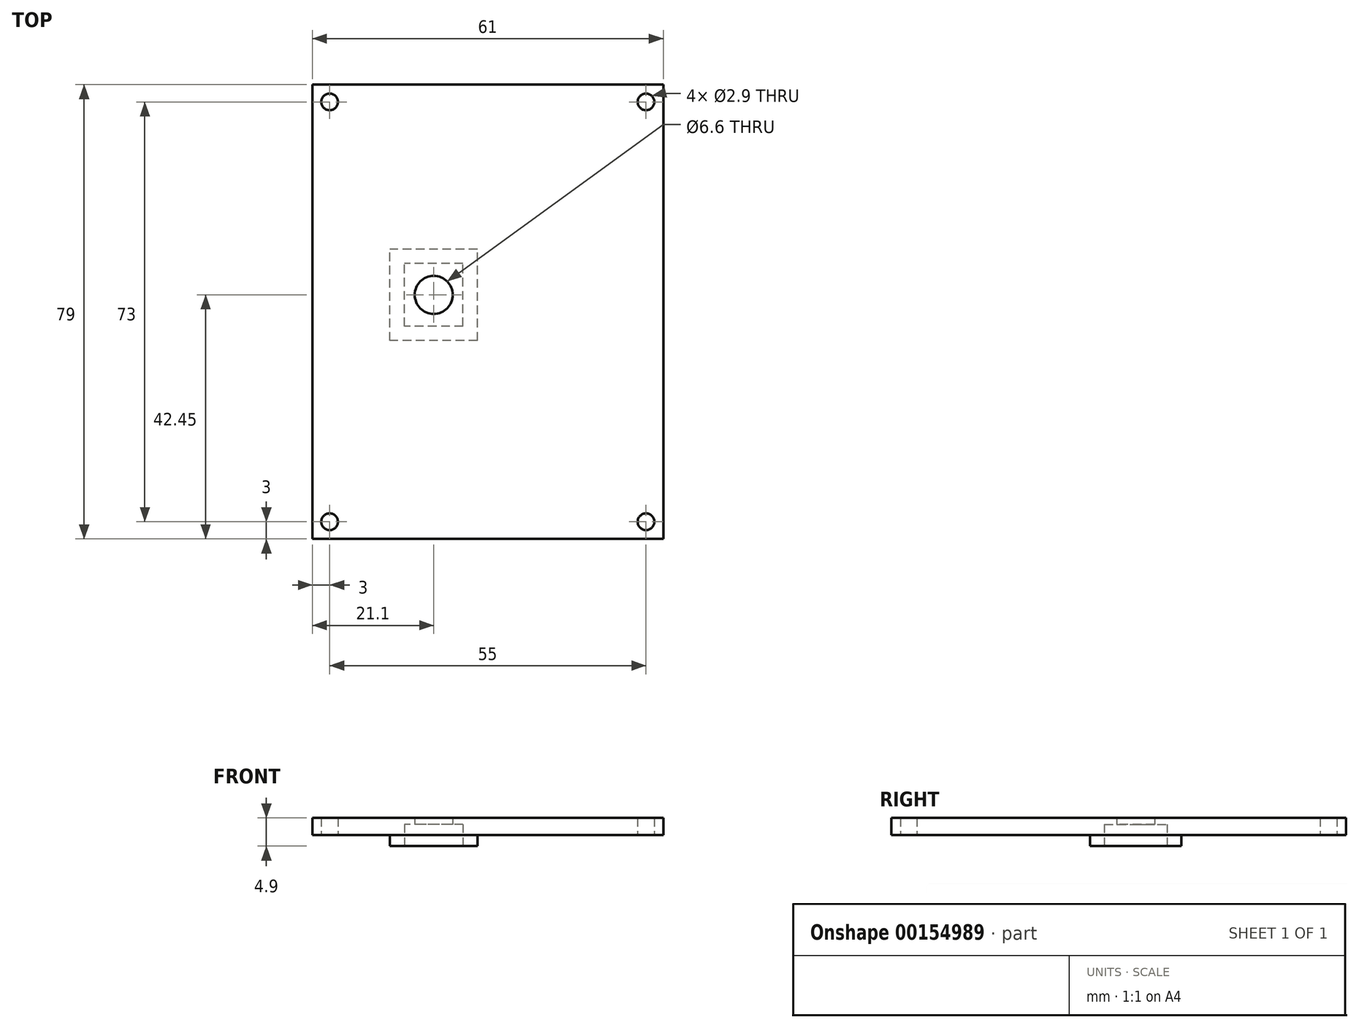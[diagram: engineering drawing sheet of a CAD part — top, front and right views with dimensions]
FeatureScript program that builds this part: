
annotation { "Feature Type Name" : "Feature", "Feature Type Description" : "" }
export const myFeature = defineFeature(function(context is Context, id is Id, definition is map)
    precondition{}
    {
        {
            var Q0;
            Q0=qCreatedBy(makeId("Top.planeOp"),FACE);
            var sketch = newSketch(context, id + "F0", { "sketchPlane" : qUnion([Q0])});
            skLineSegment(sketch, "E0.bottom", {"start": v(-30.5, 39.5) * mm, "end": v(30.5, 39.5) * mm});
            skLineSegment(sketch, "E0.top", {"start": v(-30.5, -39.5) * mm, "end": v(30.5, -39.5) * mm});
            skLineSegment(sketch, "E0.left", {"start": v(-30.5, 39.5) * mm, "end": v(-30.5, -39.5) * mm});
            skLineSegment(sketch, "E0.right", {"start": v(30.5, 39.5) * mm, "end": v(30.5, -39.5) * mm});
            skPoint(sketch, "E0.middle", {"position": v(0, 0) * mm});
            skCircle(sketch, "E1", {"center": v(-27.5, -36.5) * mm, "radius": 1.45 * mm});
            skCircle(sketch, "E2", {"center": v(27.5, -36.5) * mm, "radius": 1.45 * mm});
            skCircle(sketch, "E3", {"center": v(27.5, 36.5) * mm, "radius": 1.45 * mm});
            skCircle(sketch, "E4", {"center": v(-27.5, 36.5) * mm, "radius": 1.45 * mm});
            skLineSegment(sketch, "E5.bottom", {"start": v(-4.3, -2.5) * mm, "end": v(-14.5, -2.5) * mm});
            skLineSegment(sketch, "E5.top", {"start": v(-4.3, 8.4) * mm, "end": v(-14.5, 8.4) * mm});
            skLineSegment(sketch, "E5.left", {"start": v(-4.3, -2.5) * mm, "end": v(-4.3, 8.4) * mm});
            skLineSegment(sketch, "E5.right", {"start": v(-14.5, -2.5) * mm, "end": v(-14.5, 8.4) * mm});
            skPoint(sketch, "E5.middle", {"position": v(-9.4, 2.95) * mm});
            skLineSegment(sketch, "E6.0", {"start": v(-17, -5) * mm, "end": v(-17, 10.9) * mm});
            skLineSegment(sketch, "E6.1", {"start": v(-1.8, -5) * mm, "end": v(-17, -5) * mm});
            skLineSegment(sketch, "E6.2", {"start": v(-1.8, -5) * mm, "end": v(-1.8, 10.9) * mm});
            skLineSegment(sketch, "E6.3", {"start": v(-1.8, 10.9) * mm, "end": v(-17, 10.9) * mm});
            skCircle(sketch, "E7", {"center": v(-9.4, 2.95) * mm, "radius": 3.3 * mm});
            skSolve(sketch);
        }
        {
            var Q0;
            Q0=makeQuery(id+"F0.imprint","IMPRINT",FACE,{"disambiguationData":[TD([[makeQuery(id+"F0.imprint","IMPRINT",EDGE,{"derivedFrom":sQuery(id+"F0.wireOp",EDGE,"E0.bottom")}),-1.0]])]});
            var Q1;
            Q1=makeQuery(id+"F0.imprint","IMPRINT",FACE,{"disambiguationData":[TD([[makeQuery(id+"F0.imprint","IMPRINT",EDGE,{"derivedFrom":sQuery(id+"F0.wireOp",EDGE,"E5.bottom")}),1.0]])]});
            var Q2;
            Q2=makeQuery(id+"F0.imprint","IMPRINT",FACE,{"disambiguationData":[TD([[makeQuery(id+"F0.imprint","IMPRINT",EDGE,{"derivedFrom":sQuery(id+"F0.wireOp",EDGE,"E5.bottom")}),-1.0]])]});
            extrude(context, id + "F1", {"entities" : qUnion([Q0, Q1, Q2]), "depth" : 3 * mm});
        }
        {
            var Q0;
            Q0=makeQuery(id+"F0.imprint","IMPRINT",FACE,{"disambiguationData":[TD([[makeQuery(id+"F0.imprint","IMPRINT",EDGE,{"derivedFrom":sQuery(id+"F0.wireOp",EDGE,"E5.bottom")}),-1.0]])]});
            extrude(context, id + "F2", {"entities" : qUnion([Q0]), "operationType" : NewBodyOperationType.REMOVE, "depth" : 1.9 * mm});
        }
        {
            var Q0;
            Q0=makeQuery(id+"F0.imprint","IMPRINT",FACE,{"disambiguationData":[TD([[makeQuery(id+"F0.imprint","IMPRINT",EDGE,{"derivedFrom":sQuery(id+"F0.wireOp",EDGE,"E5.bottom")}),1.0]])]});
            extrude(context, id + "F3", {"entities" : qUnion([Q0]), "operationType" : NewBodyOperationType.ADD, "oppositeDirection" : true, "depth" : 1.9 * mm});
        }
    });
